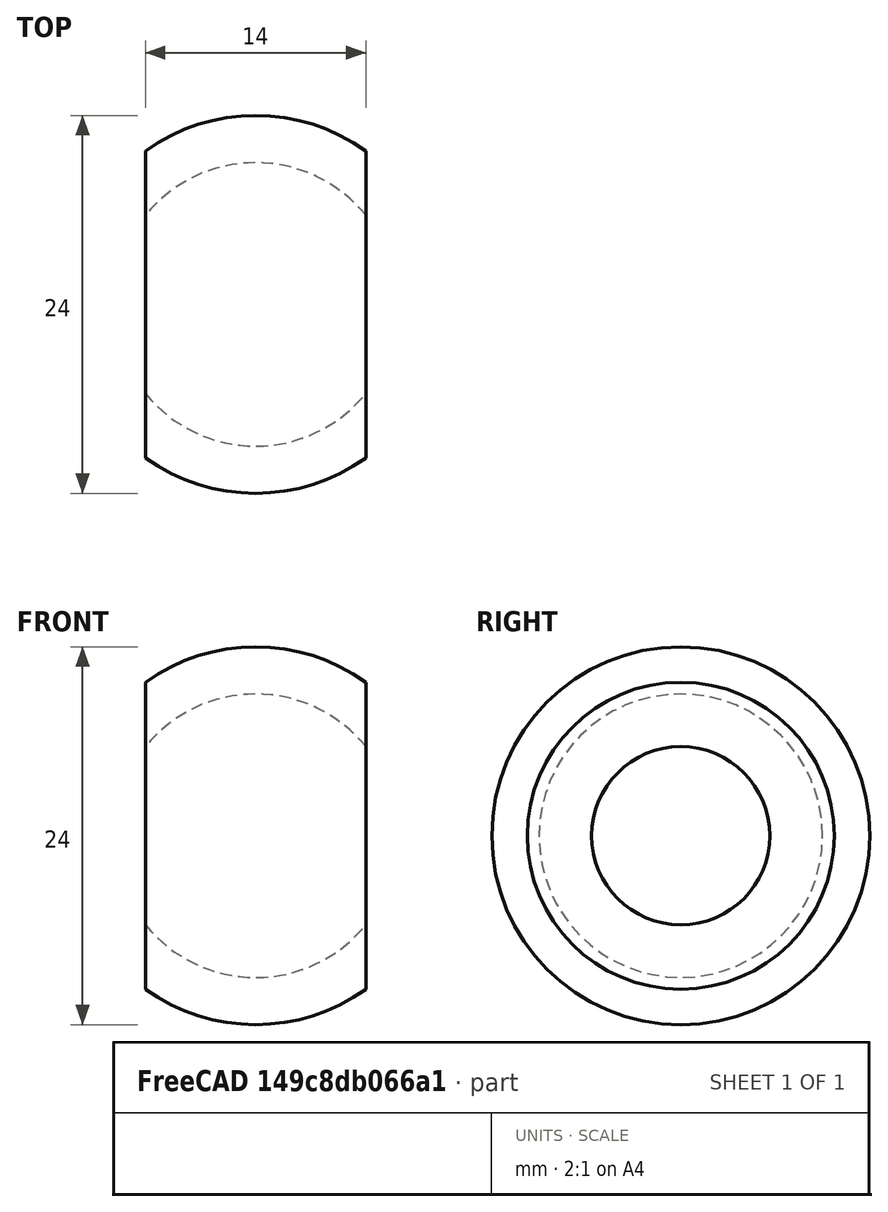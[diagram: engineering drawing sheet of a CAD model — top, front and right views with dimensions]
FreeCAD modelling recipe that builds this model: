
FCSTD DOCUMENT  (FreeCAD 0.19R24276 (Git))
Label: podvig_opora_v1
License: All rights reserved
LicenseURL: http://en.wikipedia.org/wiki/All_rights_reserved
objects: Sketcher::SketchObject×1, PartDesign::Revolution×1, PartDesign::Body×1
note: 4 computed .brp shape members not serialized (recipe doc carries the construction recipe); baked Part::Feature solids carry a one-line shape summary decoded from their .brp

FEATURE [Sketcher::SketchObject] Sketch
  FullyConstrained = false
  MapMode = 5
  Support = -> [XY_Plane]
  sketch-geometry (4):
    g0: ArcOfCircle CenterX=0 CenterY=0 CenterZ=0 NormalX=0 NormalY=0 NormalZ=1 AngleXU=0 Radius=12 StartAngle=0.94797 EndAngle=2.19362
    g1: ArcOfCircle CenterX=0 CenterY=0 CenterZ=0 NormalX=0 NormalY=0 NormalZ=1 AngleXU=0 Radius=9 StartAngle=0.679674 EndAngle=2.46192
    g2: LineSegment StartX=7 StartY=9.74679 StartZ=0 EndX=7 EndY=5.65685 EndZ=0
    g3: LineSegment StartX=-7 StartY=5.65685 StartZ=0 EndX=-7 EndY=9.74679 EndZ=0
  constraints (9):
    c: Coincident(g0,g-1)
    c: Coincident(g1,g0)
    c: Diameter(g0) = 24
    c: Diameter(g1) = 18
    c: Vertical(g2)
    c: Coincident(g2,g1)
    c: Coincident(g3,g1)
    c: Coincident(g2,g0)
    c: PointOnObject(g3,g0)
FEATURE [PartDesign::Revolution] Revolution
  Angle = 360
  Axis = (1,0,0)
  Base = (0,0,0)
  Profile = -> Sketch
  ReferenceAxis = -> Sketch [H_Axis]
FEATURE [PartDesign::Body] Body
  Group = -> [Sketch,Revolution]
  Origin = -> Origin
  Tip = -> Revolution
